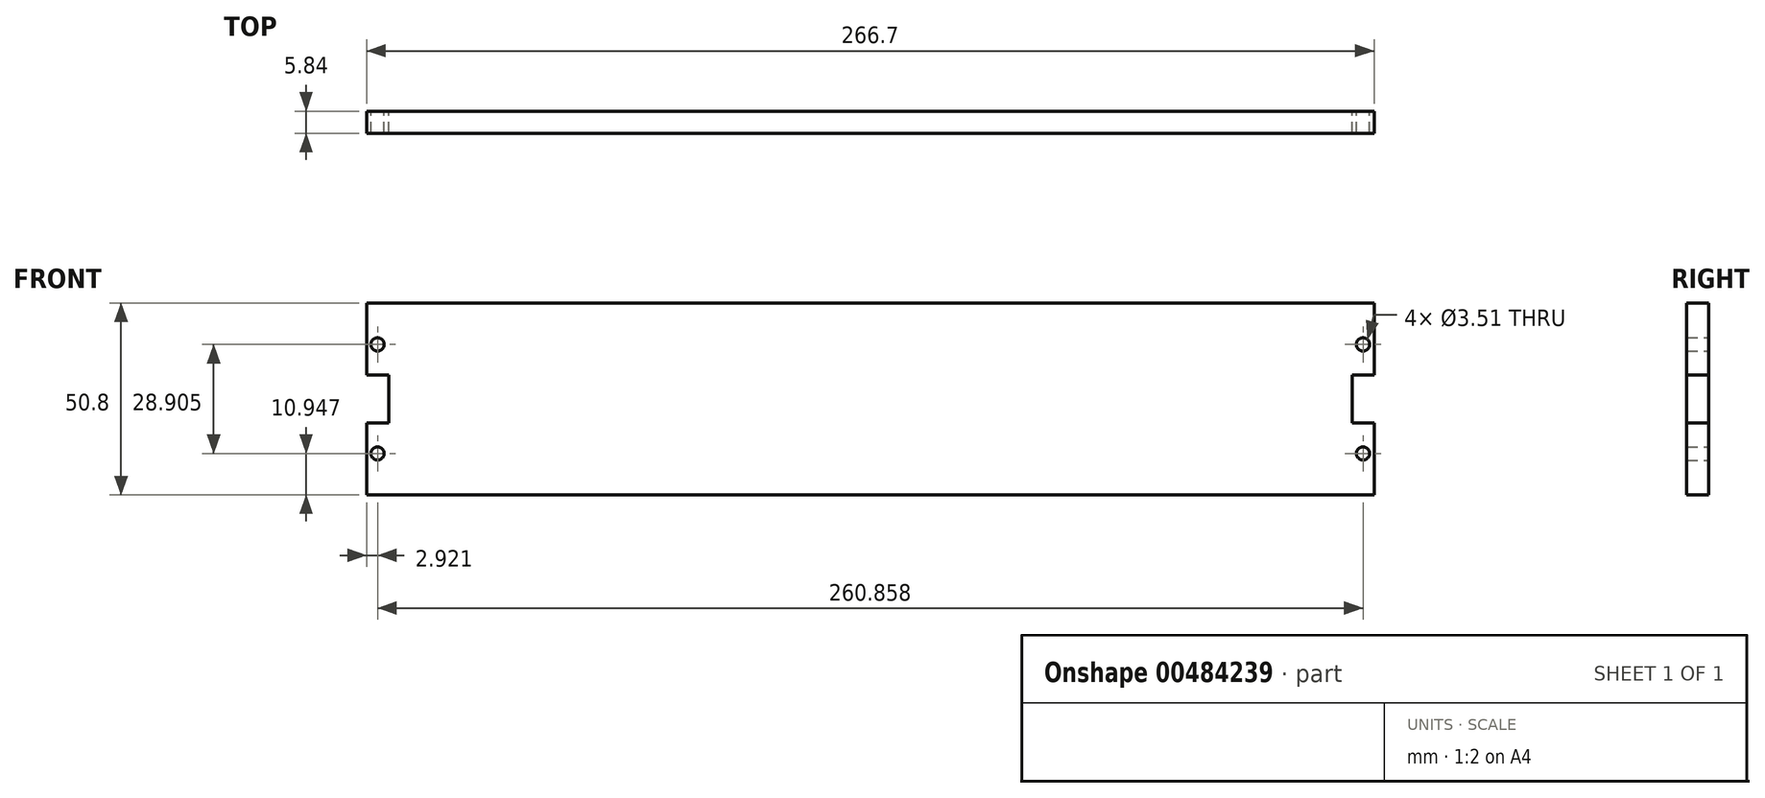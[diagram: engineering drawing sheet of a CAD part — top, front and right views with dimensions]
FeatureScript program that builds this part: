
annotation { "Feature Type Name" : "Feature", "Feature Type Description" : "" }
export const myFeature = defineFeature(function(context is Context, id is Id, definition is map)
    precondition{}
    {
        {
            var Q0;
            Q0=qCreatedBy(makeId("Front.planeOp"),FACE);
            var sketch = newSketch(context, id + "F0", { "sketchPlane" : qUnion([Q0])});
            skLineSegment(sketch, "E0.bottom", {"start": v(-133.35, 25.4) * mm, "end": v(133.35, 25.4) * mm});
            skLineSegment(sketch, "E0.top", {"start": v(-133.35, -25.4) * mm, "end": v(133.35, -25.4) * mm});
            skLineSegment(sketch, "E0.left", {"start": v(-133.35, 25.4) * mm, "end": v(-133.35, 6.35) * mm});
            skLineSegment(sketch, "E0.right", {"start": v(133.35, 25.4) * mm, "end": v(133.35, 6.35) * mm});
            skPoint(sketch, "E0.middle", {"position": v(0, 0) * mm});
            skLineSegment(sketch, "E1.bottom", {"start": v(133.35, 6.35) * mm, "end": v(127.5, 6.35) * mm});
            skLineSegment(sketch, "E1.top", {"start": v(133.35, -6.35) * mm, "end": v(127.5, -6.35) * mm});
            skLineSegment(sketch, "E1.right", {"start": v(127.5, 6.35) * mm, "end": v(127.5, -6.35) * mm});
            skPoint(sketch, "E1.middle", {"position": v(130.43, 0) * mm});
            skPoint(sketch, "E1.middle.positionSnap0", {"position": v(133.35, 0) * mm});
            skPoint(sketch, "E1.centerSnap0", {"position": v(133.35, 0) * mm});
            skLineSegment(sketch, "E2.trimOffspring", {"start": v(133.35, -6.35) * mm, "end": v(133.35, -25.4) * mm});
            skLineSegment(sketch, "E3", {"start": v(130.43, 6.35) * mm, "end": v(130.43, -6.35) * mm, "construction": true});
            skCircle(sketch, "E4", {"center": v(130.43, -14.45) * mm, "radius": 1.75 * mm});
            skCircle(sketch, "E5.MirrorC", {"center": v(130.43, 14.45) * mm, "radius": 1.75 * mm});
            skLineSegment(sketch, "E6", {"start": v(0, 25.4) * mm, "end": v(0, -25.4) * mm, "construction": true});
            skLineSegment(sketch, "E7.MirrorCS", {"start": v(-130.43, 6.35) * mm, "end": v(-130.43, -6.35) * mm, "construction": true});
            skPoint(sketch, "E8.MirrorP", {"position": v(-133.35, 0) * mm});
            skLineSegment(sketch, "E9.MirrorCS", {"start": v(-127.5, 6.35) * mm, "end": v(-127.5, -6.35) * mm});
            skPoint(sketch, "E10.MirrorP", {"position": v(-130.43, 0) * mm});
            skLineSegment(sketch, "E11.MirrorCS", {"start": v(-133.35, -6.35) * mm, "end": v(-127.5, -6.35) * mm});
            skLineSegment(sketch, "E12.MirrorCS", {"start": v(-133.35, 6.35) * mm, "end": v(-127.5, 6.35) * mm});
            skCircle(sketch, "E13.MirrorC", {"center": v(-130.43, 14.45) * mm, "radius": 1.75 * mm});
            skCircle(sketch, "E14.MirrorC", {"center": v(-130.43, -14.45) * mm, "radius": 1.75 * mm});
            skLineSegment(sketch, "E15.trimOffspring", {"start": v(-133.35, -6.35) * mm, "end": v(-133.35, -25.4) * mm});
            skSolve(sketch);
        }
        {
            var Q0;
            Q0 = qSketchRegion(id + "F0", true);
            extrude(context, id + "F1", {"entities" : qUnion([Q0]), "depth" : 5.84 * mm});
        }
    });
